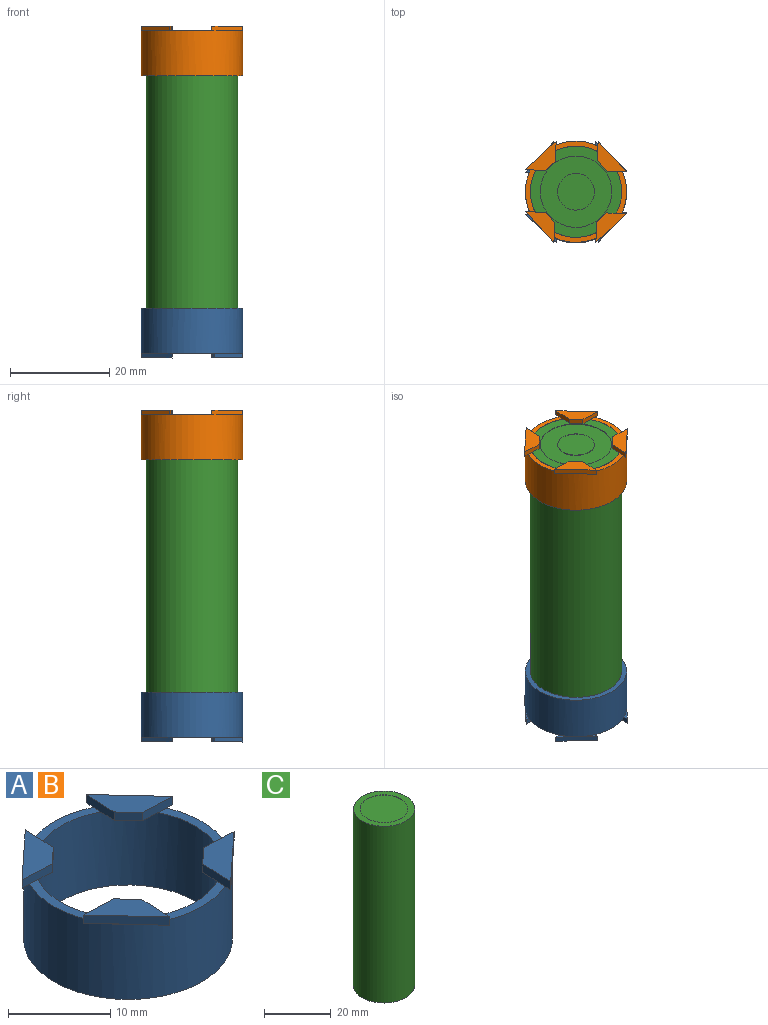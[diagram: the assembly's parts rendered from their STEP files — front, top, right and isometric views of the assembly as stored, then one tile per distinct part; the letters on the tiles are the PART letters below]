
ASSEMBLY  parts=3 mates=3
PART A: 39 faces, bbox 20.4x20.4x10 mm
  f0: plane 8.5x2.1mm, normal (0,0,1), area 8.7mm2, adj f4,f5,f27,f33
  f1: plane 8.5x2.1mm, normal (0,0,1), area 8.7mm2, adj f4,f5,f11,f35
  f2: plane 8.5x2.1mm, normal (0,0,1), area 8.7mm2, adj f4,f5,f19,f25
  f3: plane 8.5x2.1mm, normal (0,0,1), area 8.7mm2, adj f4,f5,f9,f17
  f4: cylinder r=9.2mm len=18.4mm, axis (0,0,-1), area 520.2mm2, adj f0,f1,f2,f3,f6,f14,f15,f23
  f5: cylinder r=10.2mm len=20.4mm, axis (0,0,-1), area 576.8mm2, adj f0,f1,f2,f3,f6,f7,f8,f16
  f6: plane 20.4x20.4mm, normal (0,0,-1), area 60.9mm2, adj f4,f5
  f7: plane 2.93x2.72mm, normal (0,0,-1), area 0.8mm2, adj f5,f11,f12
  f8: plane 3.27x3.07mm, normal (0,0,-1), area 1.1mm2, adj f5,f9,f12
  f9: plane 4x1mm, normal (0.04,1,0), area 4mm2, adj f3,f8,f10,f12,f13,f14
  f10: plane 2.02x1.87mm, normal (-0.68,0.73,0), area 2.8mm2, adj f9,f11,f13,f14
  f11: plane 4.05x1mm, normal (-1,0.04,0), area 4.1mm2, adj f1,f7,f10,f12,f13,f14
  f12: plane 6.2x5.75mm, normal (0.68,-0.73,0), area 8.5mm2, adj f7,f8,f9,f11,f13
  f13: plane 6.2x5.92mm, normal (0,0,1), area 16mm2, adj f9,f10,f11,f12
  f14: plane 4.01x3.97mm, normal (0,0,-1), area 7.5mm2, adj f4,f9,f10,f11
  f15: plane 4.01x3.97mm, normal (0,0,-1), area 7.5mm2, adj f4,f17,f19,f20
  f16: plane 2.93x2.72mm, normal (0,0,-1), area 0.8mm2, adj f5,f17,f18
  f17: plane 4.05x1mm, normal (-0.04,-1,0), area 4.1mm2, adj f3,f15,f16,f18,f20,f21
  f18: plane 6.2x5.75mm, normal (0.73,0.68,0), area 8.5mm2, adj f16,f17,f19,f21,f22
  f19: plane 4x1mm, normal (-1,0.04,0), area 4mm2, adj f2,f15,f18,f20,f21,f22
  f20: plane 2.02x1.87mm, normal (-0.73,-0.68,0), area 2.8mm2, adj f15,f17,f19,f21
  f21: plane 6.2x5.92mm, normal (0,0,1), area 16mm2, adj f17,f18,f19,f20
  f22: plane 3.27x3.07mm, normal (0,0,-1), area 1.1mm2, adj f5,f18,f19
  f23: plane 4.01x3.97mm, normal (0,0,-1), area 7.5mm2, adj f4,f25,f27,f28
  f24: plane 2.93x2.72mm, normal (0,0,-1), area 0.8mm2, adj f5,f25,f26
  f25: plane 4.05x1mm, normal (1,-0.04,0), area 4.1mm2, adj f2,f23,f24,f26,f28,f29
  f26: plane 6.2x5.75mm, normal (-0.68,0.73,0), area 8.5mm2, adj f24,f25,f27,f29,f30
  f27: plane 4x1mm, normal (-0.04,-1,0), area 4mm2, adj f0,f23,f26,f28,f29,f30
  f28: plane 2.02x1.87mm, normal (0.68,-0.73,0), area 2.8mm2, adj f23,f25,f27,f29
  f29: plane 6.2x5.92mm, normal (0,0,1), area 16mm2, adj f25,f26,f27,f28
  f30: plane 3.27x3.07mm, normal (0,0,-1), area 1.1mm2, adj f5,f26,f27
  f31: plane 4.01x3.97mm, normal (0,0,-1), area 7.5mm2, adj f4,f33,f35,f36
  f32: plane 2.93x2.72mm, normal (0,0,-1), area 0.8mm2, adj f5,f33,f34
  f33: plane 4.05x1mm, normal (0.04,1,0), area 4.1mm2, adj f0,f31,f32,f34,f36,f37
  f34: plane 6.2x5.75mm, normal (-0.73,-0.68,0), area 8.5mm2, adj f32,f33,f35,f37,f38
  f35: plane 4x1mm, normal (1,-0.04,0), area 4mm2, adj f1,f31,f34,f36,f37,f38
  f36: plane 2.02x1.87mm, normal (0.73,0.68,0), area 2.8mm2, adj f31,f33,f35,f37
  f37: plane 6.2x5.92mm, normal (0,0,1), area 16mm2, adj f33,f34,f35,f36
  f38: plane 3.27x3.07mm, normal (0,0,-1), area 1.1mm2, adj f5,f34,f35
PART B: same geometry as A
PART C: 9 faces, bbox 18.4x18.4x65 mm
  f0: cylinder r=9.2mm len=65mm, axis (0,0,-1), area 3757.3mm2, adj f1,f7
  f1: plane 18.4x18.4mm, normal (0,0,-1), area 103mm2, adj f0,f3
  f2: cylinder r=3.7mm len=7.4mm, axis (0,0,-1), area 2.3mm2, adj f4,f5
  f3: cylinder r=7.2mm len=14.4mm, axis (0,0,-1), area 4.5mm2, adj f1,f4
  f4: plane 14.4x14.4mm, normal (0,0,-1), area 119.9mm2, adj f2,f3
  f5: plane 7.4x7.4mm, normal (0,0,-1), area 43mm2, adj f2
  f6: cylinder r=7.2mm len=14.4mm, axis (0,0,-1), area 4.5mm2, adj f7,f8
  f7: plane 18.4x18.4mm, normal (0,0,1), area 103mm2, adj f0,f6
  f8: plane 14.4x14.4mm, normal (0,0,1), area 162.9mm2, adj f6
PLACE A rot(axis=(-1,0,0),180deg) t=(-25.71,9.44,-50.65)mm
PLACE B rot(axis=(0.75,-0.52,0.42),0deg) t=(-25.71,9.44,-3.75)mm
PLACE C rot(axis=(0,1,0),180deg) t=(-25.71,9.44,5.25)mm
MATE fastened C.f0 <-> B.f5  axis (0,0,1) through (-25.71,9.44,5.25)mm
MATE fastened C.f0 <-> B.f4  axis (0,0,1) through (-25.71,9.44,-59.75)mm
MATE fastened A.f5 <-> C.f3  axis (0,0,1) through (-25.71,9.44,-59.65)mm
